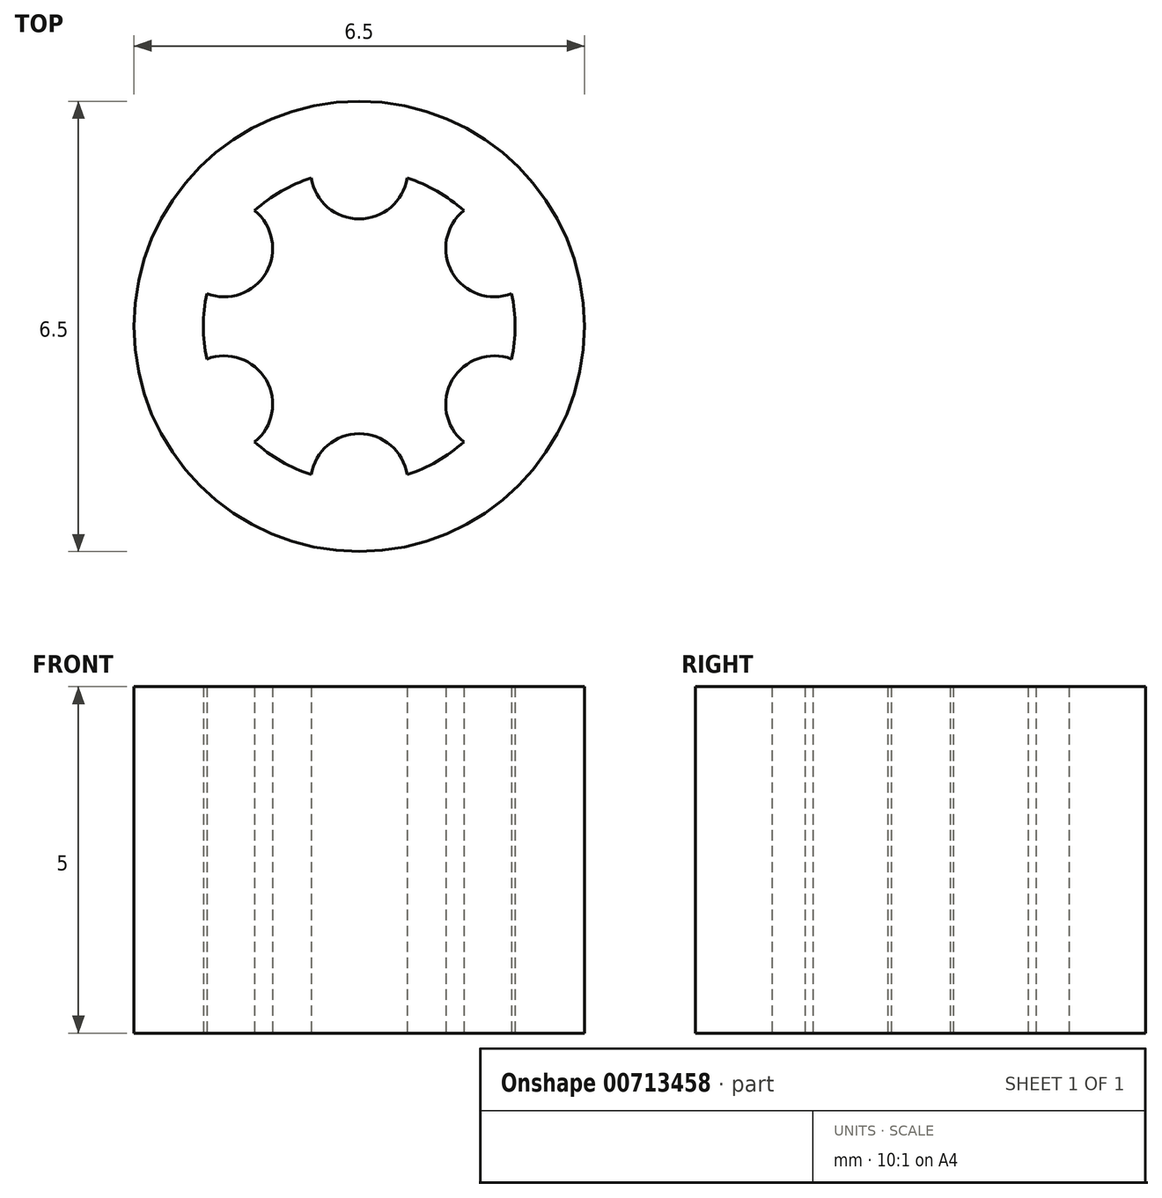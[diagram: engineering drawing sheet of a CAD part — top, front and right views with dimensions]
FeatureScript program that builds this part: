
annotation { "Feature Type Name" : "Feature", "Feature Type Description" : "" }
export const myFeature = defineFeature(function(context is Context, id is Id, definition is map)
    precondition{}
    {
        {
            var Q0;
            Q0=qCreatedBy(makeId("Top.planeOp"),FACE);
            var sketch = newSketch(context, id + "F0", { "sketchPlane" : qUnion([Q0])});
            skCircle(sketch, "E0", {"center": v(0, 0) * mm, "radius": 2.25 * mm});
            skCircle(sketch, "E1", {"center": v(0, 0) * mm, "radius": 3.25 * mm});
            skCircle(sketch, "E2", {"center": v(0, 2.25) * mm, "radius": 0.7 * mm});
            skCircle(sketch, "E3.1.0", {"center": v(-1.95, 1.13) * mm, "radius": 0.7 * mm});
            skCircle(sketch, "E3.2.0", {"center": v(-1.95, -1.12) * mm, "radius": 0.7 * mm});
            skCircle(sketch, "E3.3.0", {"center": v(0, -2.25) * mm, "radius": 0.7 * mm});
            skCircle(sketch, "E3.4.0", {"center": v(1.95, -1.13) * mm, "radius": 0.7 * mm});
            skCircle(sketch, "E3.5.0", {"center": v(1.95, 1.13) * mm, "radius": 0.7 * mm});
            skSolve(sketch);
        }
        {
            var Q0;
            Q0 = qSketchRegion(id + "F0", true);
            var Q1;
            {var subQ0=sQuery(id+"F0.wireOp",EDGE,"E3.1.0");var subQ1=sQuery(id+"F0.wireOp",EDGE,"E0");var subQ2=makeQuery(id+"F0.imprint","INTERSECT",VERTEX,{"disambiguationData":[OD(0.0)],"derivedFrom":[subQ1,subQ0]});Q1=makeQuery(id+"F0.imprint","IMPRINT",FACE,{"disambiguationData":[TD([[makeQuery(id+"F0.imprint","IMPRINT",EDGE,{"disambiguationData":[TD([[subQ2,-1.0]])],"derivedFrom":subQ1}),1.0]])]});}
            var Q2;
            {var subQ0=sQuery(id+"F0.wireOp",EDGE,"E3.1.0");var subQ1=sQuery(id+"F0.wireOp",EDGE,"E0");var subQ2=makeQuery(id+"F0.imprint","INTERSECT",VERTEX,{"disambiguationData":[OD(0.0)],"derivedFrom":[subQ1,subQ0]});Q2=makeQuery(id+"F0.imprint","IMPRINT",FACE,{"disambiguationData":[TD([[makeQuery(id+"F0.imprint","IMPRINT",EDGE,{"disambiguationData":[TD([[subQ2,-1.0]])],"derivedFrom":subQ1}),-1.0]])]});}
            var Q3;
            {var subQ0=sQuery(id+"F0.wireOp",EDGE,"E2");var subQ1=sQuery(id+"F0.wireOp",EDGE,"E0");var subQ2=makeQuery(id+"F0.imprint","INTERSECT",VERTEX,{"disambiguationData":[OD(0.0)],"derivedFrom":[subQ1,subQ0]});Q3=makeQuery(id+"F0.imprint","IMPRINT",FACE,{"disambiguationData":[TD([[makeQuery(id+"F0.imprint","IMPRINT",EDGE,{"disambiguationData":[TD([[subQ2,-1.0]])],"derivedFrom":subQ1}),-1.0]])]});}
            var Q4;
            {var subQ0=sQuery(id+"F0.wireOp",EDGE,"E2");var subQ1=sQuery(id+"F0.wireOp",EDGE,"E0");var subQ2=makeQuery(id+"F0.imprint","INTERSECT",VERTEX,{"disambiguationData":[OD(0.0)],"derivedFrom":[subQ1,subQ0]});Q4=makeQuery(id+"F0.imprint","IMPRINT",FACE,{"disambiguationData":[TD([[makeQuery(id+"F0.imprint","IMPRINT",EDGE,{"disambiguationData":[TD([[subQ2,-1.0]])],"derivedFrom":subQ1}),1.0]])]});}
            var Q5;
            {var subQ0=sQuery(id+"F0.wireOp",EDGE,"E3.5.0");var subQ1=sQuery(id+"F0.wireOp",EDGE,"E0");var subQ2=makeQuery(id+"F0.imprint","INTERSECT",VERTEX,{"disambiguationData":[OD(0.0)],"derivedFrom":[subQ1,subQ0]});Q5=makeQuery(id+"F0.imprint","IMPRINT",FACE,{"disambiguationData":[TD([[makeQuery(id+"F0.imprint","IMPRINT",EDGE,{"disambiguationData":[TD([[subQ2,1.0]])],"derivedFrom":subQ1}),-1.0]])]});}
            var Q6;
            {var subQ0=sQuery(id+"F0.wireOp",EDGE,"E3.5.0");var subQ1=sQuery(id+"F0.wireOp",EDGE,"E0");var subQ2=makeQuery(id+"F0.imprint","INTERSECT",VERTEX,{"disambiguationData":[OD(0.0)],"derivedFrom":[subQ1,subQ0]});Q6=makeQuery(id+"F0.imprint","IMPRINT",FACE,{"disambiguationData":[TD([[makeQuery(id+"F0.imprint","IMPRINT",EDGE,{"disambiguationData":[TD([[subQ2,1.0]])],"derivedFrom":subQ1}),1.0]])]});}
            var Q7;
            {var subQ0=sQuery(id+"F0.wireOp",EDGE,"E3.4.0");var subQ1=sQuery(id+"F0.wireOp",EDGE,"E0");var subQ2=makeQuery(id+"F0.imprint","INTERSECT",VERTEX,{"disambiguationData":[OD(0.0)],"derivedFrom":[subQ1,subQ0]});Q7=makeQuery(id+"F0.imprint","IMPRINT",FACE,{"disambiguationData":[TD([[makeQuery(id+"F0.imprint","IMPRINT",EDGE,{"disambiguationData":[TD([[subQ2,-1.0]])],"derivedFrom":subQ1}),-1.0]])]});}
            var Q8;
            {var subQ0=sQuery(id+"F0.wireOp",EDGE,"E3.3.0");var subQ1=sQuery(id+"F0.wireOp",EDGE,"E0");var subQ2=makeQuery(id+"F0.imprint","INTERSECT",VERTEX,{"disambiguationData":[OD(0.0)],"derivedFrom":[subQ1,subQ0]});Q8=makeQuery(id+"F0.imprint","IMPRINT",FACE,{"disambiguationData":[TD([[makeQuery(id+"F0.imprint","IMPRINT",EDGE,{"disambiguationData":[TD([[subQ2,-1.0]])],"derivedFrom":subQ1}),-1.0]])]});}
            var Q9;
            {var subQ0=sQuery(id+"F0.wireOp",EDGE,"E3.2.0");var subQ1=sQuery(id+"F0.wireOp",EDGE,"E0");var subQ2=makeQuery(id+"F0.imprint","INTERSECT",VERTEX,{"disambiguationData":[OD(0.0)],"derivedFrom":[subQ1,subQ0]});Q9=makeQuery(id+"F0.imprint","IMPRINT",FACE,{"disambiguationData":[TD([[makeQuery(id+"F0.imprint","IMPRINT",EDGE,{"disambiguationData":[TD([[subQ2,-1.0]])],"derivedFrom":subQ1}),-1.0]])]});}
            var Q10;
            {var subQ0=sQuery(id+"F0.wireOp",EDGE,"E3.3.0");var subQ1=sQuery(id+"F0.wireOp",EDGE,"E0");var subQ2=makeQuery(id+"F0.imprint","INTERSECT",VERTEX,{"disambiguationData":[OD(0.0)],"derivedFrom":[subQ1,subQ0]});Q10=makeQuery(id+"F0.imprint","IMPRINT",FACE,{"disambiguationData":[TD([[makeQuery(id+"F0.imprint","IMPRINT",EDGE,{"disambiguationData":[TD([[subQ2,-1.0]])],"derivedFrom":subQ1}),1.0]])]});}
            var Q11;
            {var subQ0=sQuery(id+"F0.wireOp",EDGE,"E3.2.0");var subQ1=sQuery(id+"F0.wireOp",EDGE,"E0");var subQ2=makeQuery(id+"F0.imprint","INTERSECT",VERTEX,{"disambiguationData":[OD(0.0)],"derivedFrom":[subQ1,subQ0]});Q11=makeQuery(id+"F0.imprint","IMPRINT",FACE,{"disambiguationData":[TD([[makeQuery(id+"F0.imprint","IMPRINT",EDGE,{"disambiguationData":[TD([[subQ2,-1.0]])],"derivedFrom":subQ1}),1.0]])]});}
            var Q12;
            {var subQ0=sQuery(id+"F0.wireOp",EDGE,"E3.4.0");var subQ1=sQuery(id+"F0.wireOp",EDGE,"E0");var subQ2=makeQuery(id+"F0.imprint","INTERSECT",VERTEX,{"disambiguationData":[OD(0.0)],"derivedFrom":[subQ1,subQ0]});Q12=makeQuery(id+"F0.imprint","IMPRINT",FACE,{"disambiguationData":[TD([[makeQuery(id+"F0.imprint","IMPRINT",EDGE,{"disambiguationData":[TD([[subQ2,-1.0]])],"derivedFrom":subQ1}),1.0]])]});}
            extrude(context, id + "F1", {"entities" : qUnion([Q0, Q1, Q2, Q3, Q4, Q5, Q6, Q7, Q8, Q9, Q10, Q11, Q12]), "depth" : 5 * mm, "offsetDistance" : 25 * mm});
        }
    });
